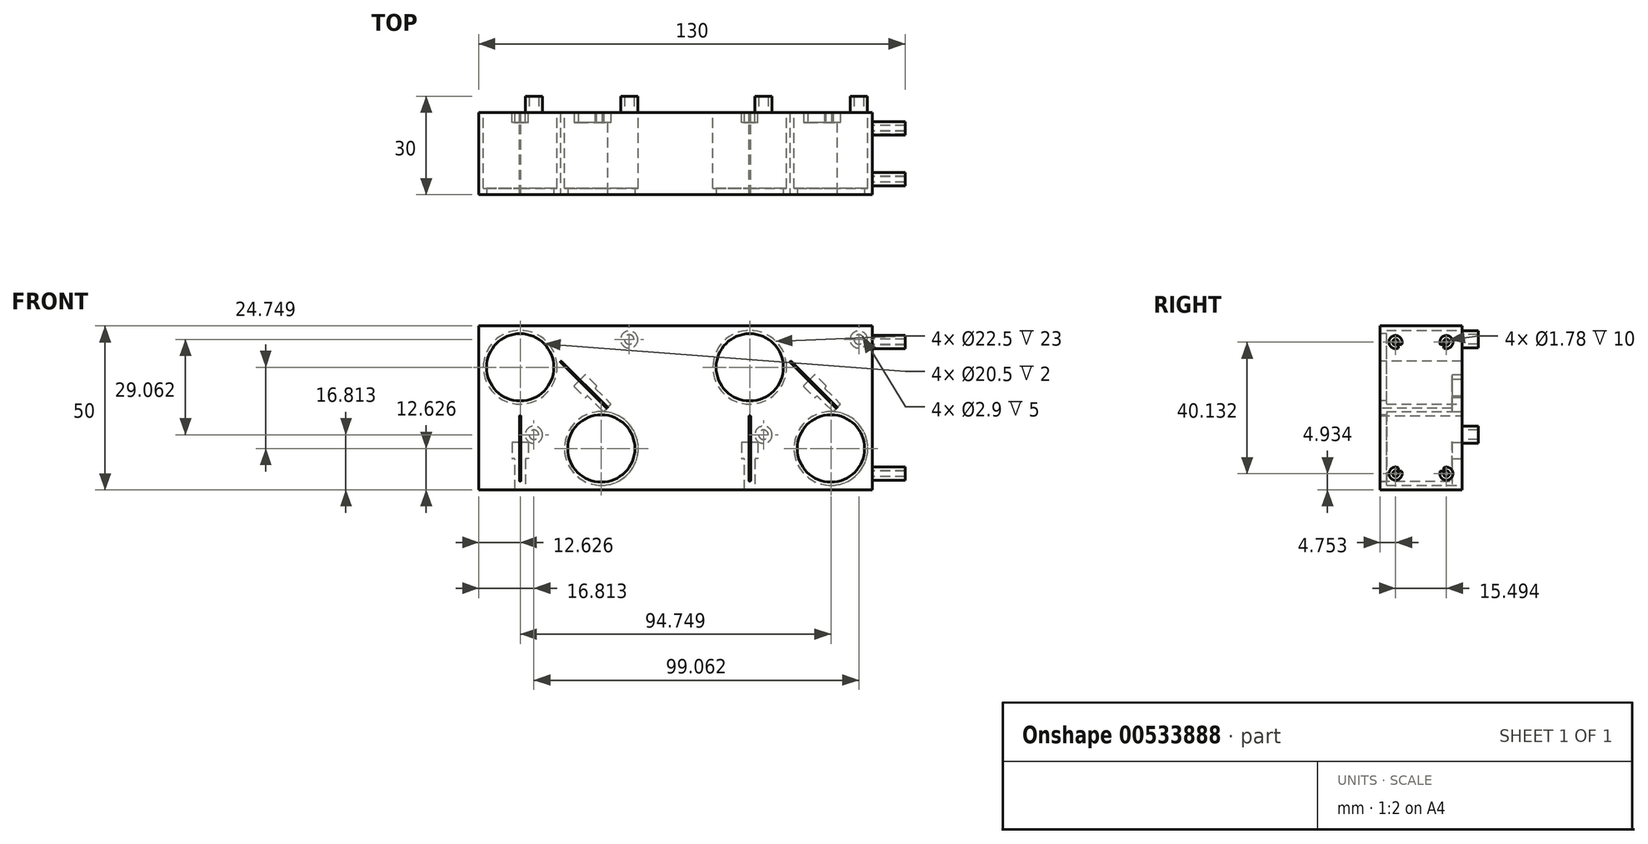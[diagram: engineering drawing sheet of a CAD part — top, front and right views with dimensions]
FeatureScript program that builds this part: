
annotation { "Feature Type Name" : "Feature", "Feature Type Description" : "" }
export const myFeature = defineFeature(function(context is Context, id is Id, definition is map)
    precondition{}
    {
        {
            var Q0;
            Q0=qCreatedBy(makeId("Front.planeOp"),FACE);
            var sketch = newSketch(context, id + "F0", { "sketchPlane" : qUnion([Q0])});
            skLineSegment(sketch, "E0.bottom", {"start": v(-60, 25) * mm, "end": v(60, 25) * mm});
            skLineSegment(sketch, "E0.top", {"start": v(-60, -25) * mm, "end": v(60, -25) * mm});
            skLineSegment(sketch, "E0.left", {"start": v(-60, 25) * mm, "end": v(-60, -25) * mm});
            skLineSegment(sketch, "E0.right", {"start": v(60, 25) * mm, "end": v(60, -25) * mm});
            skPoint(sketch, "E1", {"position": v(-60, 0) * mm});
            skPoint(sketch, "E2", {"position": v(0, 25) * mm});
            skLineSegment(sketch, "E3", {"start": v(0, 25) * mm, "end": v(0, -25) * mm, "construction": true});
            skCircle(sketch, "E4", {"center": v(-47.37, 12.37) * mm, "radius": 11.25 * mm});
            skCircle(sketch, "E5", {"center": v(-22.63, -12.37) * mm, "radius": 11.25 * mm});
            skLineSegment(sketch, "E6", {"start": v(-47.37, 12.37) * mm, "end": v(-22.63, -12.37) * mm, "construction": true});
            skPoint(sketch, "E7", {"position": v(-35, 0) * mm});
            skLineSegment(sketch, "E8.bottom", {"start": v(-47.62, -2.37) * mm, "end": v(-47.12, -2.37) * mm});
            skLineSegment(sketch, "E8.top", {"start": v(-47.62, -22.37) * mm, "end": v(-47.12, -22.37) * mm});
            skLineSegment(sketch, "E8.left", {"start": v(-47.62, -2.37) * mm, "end": v(-47.62, -22.37) * mm});
            skLineSegment(sketch, "E8.right", {"start": v(-47.12, -2.37) * mm, "end": v(-47.12, -22.37) * mm});
            skLineSegment(sketch, "E9", {"start": v(-35.18, 13.97) * mm, "end": v(-34.82, 14.32) * mm});
            skLineSegment(sketch, "E10", {"start": v(-34.82, 14.32) * mm, "end": v(-20.68, 0.18) * mm});
            skLineSegment(sketch, "E11", {"start": v(-20.68, 0.18) * mm, "end": v(-21.03, -0.18) * mm});
            skLineSegment(sketch, "E12", {"start": v(-21.03, -0.18) * mm, "end": v(-35.18, 13.97) * mm});
            skLineSegment(sketch, "E13", {"start": v(-35, 14.14) * mm, "end": v(-20.86, 0) * mm, "construction": true});
            skLineSegment(sketch, "E14", {"start": v(-47.37, -2.37) * mm, "end": v(-47.37, -22.37) * mm, "construction": true});
            skLineSegment(sketch, "E15", {"start": v(-35, 0) * mm, "end": v(-27.93, 7.07) * mm, "construction": true});
            skPoint(sketch, "E16", {"position": v(-47.37, -12.37) * mm});
            skCircle(sketch, "E17.1.0.0", {"center": v(22.63, 12.37) * mm, "radius": 11.25 * mm});
            skLineSegment(sketch, "E17.1.0.1", {"start": v(22.88, -2.37) * mm, "end": v(22.88, -22.37) * mm});
            skLineSegment(sketch, "E17.1.0.2", {"start": v(22.38, -2.37) * mm, "end": v(22.38, -22.37) * mm});
            skLineSegment(sketch, "E17.1.0.3", {"start": v(22.38, -22.37) * mm, "end": v(22.88, -22.37) * mm});
            skLineSegment(sketch, "E17.1.0.4", {"start": v(22.38, -2.37) * mm, "end": v(22.88, -2.37) * mm});
            skLineSegment(sketch, "E17.1.0.5", {"start": v(35.18, 14.32) * mm, "end": v(49.32, 0.18) * mm});
            skLineSegment(sketch, "E17.1.0.6", {"start": v(48.97, -0.18) * mm, "end": v(34.82, 13.97) * mm});
            skLineSegment(sketch, "E17.1.0.7", {"start": v(34.82, 13.97) * mm, "end": v(35.18, 14.32) * mm});
            skLineSegment(sketch, "E17.1.0.8", {"start": v(49.32, 0.18) * mm, "end": v(48.97, -0.18) * mm});
            skCircle(sketch, "E17.1.0.9", {"center": v(47.37, -12.37) * mm, "radius": 11.25 * mm});
            skLineSegment(sketch, "E17.direction1", {"start": v(-47.62, -22.37) * mm, "end": v(22.38, -22.37) * mm, "construction": true});
            skSolve(sketch);
        }
        {
            var Q0;
            Q0 = qSketchRegion(id + "F0", true);
            extrude(context, id + "F1", {"entities" : qUnion([Q0]), "depth" : 25 * mm, "offsetDistance" : 25 * mm});
        }
        {
            var Q0;
            Q0=makeQuery(id+"F1.opExtrude","CAP_FACE",FACE,{"disambiguationData":[OSD([sQuery(id+"F0.wireOp",EDGE,"E0.bottom"),sQuery(id+"F0.wireOp",EDGE,"E0.top"),sQuery(id+"F0.wireOp",EDGE,"E0.left"),sQuery(id+"F0.wireOp",EDGE,"E0.right"),sQuery(id+"F0.wireOp",EDGE,"E4"),sQuery(id+"F0.wireOp",EDGE,"E5"),sQuery(id+"F0.wireOp",EDGE,"E8.bottom"),sQuery(id+"F0.wireOp",EDGE,"E8.top"),sQuery(id+"F0.wireOp",EDGE,"E8.left"),sQuery(id+"F0.wireOp",EDGE,"E8.right"),sQuery(id+"F0.wireOp",EDGE,"E9"),sQuery(id+"F0.wireOp",EDGE,"E10"),sQuery(id+"F0.wireOp",EDGE,"E11"),sQuery(id+"F0.wireOp",EDGE,"E12"),sQuery(id+"F0.wireOp",EDGE,"E17.1.0.0"),sQuery(id+"F0.wireOp",EDGE,"E17.1.0.1"),sQuery(id+"F0.wireOp",EDGE,"E17.1.0.2"),sQuery(id+"F0.wireOp",EDGE,"E17.1.0.3"),sQuery(id+"F0.wireOp",EDGE,"E17.1.0.4"),sQuery(id+"F0.wireOp",EDGE,"E17.1.0.5"),sQuery(id+"F0.wireOp",EDGE,"E17.1.0.6"),sQuery(id+"F0.wireOp",EDGE,"E17.1.0.7"),sQuery(id+"F0.wireOp",EDGE,"E17.1.0.8"),sQuery(id+"F0.wireOp",EDGE,"E17.1.0.9")])],"isStart":false});
            var sketch = newSketch(context, id + "F2", { "sketchPlane" : qUnion([Q0])});
            skCircle(sketch, "E18.0", {"center": v(-47.37, 12.37) * mm, "radius": 11.25 * mm});
            skCircle(sketch, "E18.1", {"center": v(-22.63, -12.37) * mm, "radius": 11.25 * mm});
            skCircle(sketch, "E18.2", {"center": v(22.63, 12.37) * mm, "radius": 11.25 * mm});
            skCircle(sketch, "E18.3", {"center": v(47.37, -12.37) * mm, "radius": 11.25 * mm});
            skCircle(sketch, "E19", {"center": v(-47.37, 12.37) * mm, "radius": 10.25 * mm});
            skCircle(sketch, "E20", {"center": v(-22.63, -12.37) * mm, "radius": 10.25 * mm});
            skCircle(sketch, "E21", {"center": v(22.63, 12.37) * mm, "radius": 10.25 * mm});
            skCircle(sketch, "E22", {"center": v(47.37, -12.37) * mm, "radius": 10.25 * mm});
            skSolve(sketch);
        }
        {
            var Q0;
            Q0 = qSketchRegion(id + "F2", true);
            extrude(context, id + "F3", {"entities" : qUnion([Q0]), "operationType" : NewBodyOperationType.ADD, "oppositeDirection" : true, "depth" : 2 * mm, "offsetDistance" : 25 * mm});
        }
        {
            var Q0;
            Q0=makeQuery(id+"F1.opExtrude","CAP_FACE",FACE,{"disambiguationData":[OSD([sQuery(id+"F0.wireOp",EDGE,"E0.bottom"),sQuery(id+"F0.wireOp",EDGE,"E0.top"),sQuery(id+"F0.wireOp",EDGE,"E0.left"),sQuery(id+"F0.wireOp",EDGE,"E0.right"),sQuery(id+"F0.wireOp",EDGE,"E4"),sQuery(id+"F0.wireOp",EDGE,"E5"),sQuery(id+"F0.wireOp",EDGE,"E8.bottom"),sQuery(id+"F0.wireOp",EDGE,"E8.top"),sQuery(id+"F0.wireOp",EDGE,"E8.left"),sQuery(id+"F0.wireOp",EDGE,"E8.right"),sQuery(id+"F0.wireOp",EDGE,"E9"),sQuery(id+"F0.wireOp",EDGE,"E10"),sQuery(id+"F0.wireOp",EDGE,"E11"),sQuery(id+"F0.wireOp",EDGE,"E12"),sQuery(id+"F0.wireOp",EDGE,"E17.1.0.0"),sQuery(id+"F0.wireOp",EDGE,"E17.1.0.1"),sQuery(id+"F0.wireOp",EDGE,"E17.1.0.2"),sQuery(id+"F0.wireOp",EDGE,"E17.1.0.3"),sQuery(id+"F0.wireOp",EDGE,"E17.1.0.4"),sQuery(id+"F0.wireOp",EDGE,"E17.1.0.5"),sQuery(id+"F0.wireOp",EDGE,"E17.1.0.6"),sQuery(id+"F0.wireOp",EDGE,"E17.1.0.7"),sQuery(id+"F0.wireOp",EDGE,"E17.1.0.8"),sQuery(id+"F0.wireOp",EDGE,"E17.1.0.9")])],"isStart":true});
            var sketch = newSketch(context, id + "F4", { "sketchPlane" : qUnion([Q0])});
            skLineSegment(sketch, "E23.bottom", {"start": v(-25.13, -10.47) * mm, "end": v(-20.13, -10.47) * mm});
            skLineSegment(sketch, "E23.top", {"start": v(-25.13, -15.47) * mm, "end": v(-24.25, -15.47) * mm});
            skLineSegment(sketch, "E23.left", {"start": v(-25.13, -10.47) * mm, "end": v(-25.13, -15.47) * mm});
            skLineSegment(sketch, "E23.right", {"start": v(-20.13, -10.47) * mm, "end": v(-20.13, -15.47) * mm});
            skLineSegment(sketch, "E24", {"start": v(-20.13, -10.47) * mm, "end": v(-25.13, -15.47) * mm, "construction": true});
            skPoint(sketch, "E25", {"position": v(-22.63, -12.97) * mm});
            skLineSegment(sketch, "E26", {"start": v(-24.25, -15.47) * mm, "end": v(-24.25, -25) * mm});
            skLineSegment(sketch, "E27", {"start": v(-24.25, -25) * mm, "end": v(-21, -25) * mm});
            skLineSegment(sketch, "E28", {"start": v(-21, -25) * mm, "end": v(-21, -15.47) * mm});
            skLineSegment(sketch, "E29", {"start": v(-22.63, -12.97) * mm, "end": v(-22.63, -25) * mm, "construction": true});
            skLineSegment(sketch, "E30.trimOffspring", {"start": v(-21, -15.47) * mm, "end": v(-20.13, -15.47) * mm});
            skCircle(sketch, "E31", {"center": v(-22.63, -12.37) * mm, "radius": 0.75 * mm, "construction": true});
            skLineSegment(sketch, "E32", {"start": v(-22.63, -2.37) * mm, "end": v(-22.63, -22.37) * mm, "construction": true});
            skLineSegment(sketch, "E33", {"start": v(-42.5, 10.18) * mm, "end": v(-38.96, 6.65) * mm});
            skLineSegment(sketch, "E34", {"start": v(-38.96, 6.65) * mm, "end": v(-42.5, 3.11) * mm});
            skLineSegment(sketch, "E35", {"start": v(-46.03, 6.65) * mm, "end": v(-42.5, 10.18) * mm});
            skLineSegment(sketch, "E36", {"start": v(-35, 14.14) * mm, "end": v(-49.14, 0) * mm, "construction": true});
            skPoint(sketch, "E37", {"position": v(-40.73, 8.41) * mm});
            skLineSegment(sketch, "E38", {"start": v(-46.03, 6.65) * mm, "end": v(-45.41, 6.03) * mm});
            skLineSegment(sketch, "E39", {"start": v(-45.41, 6.03) * mm, "end": v(-50.3, 1.15) * mm});
            skLineSegment(sketch, "E40", {"start": v(-50.3, 1.15) * mm, "end": v(-48, -1.15) * mm});
            skLineSegment(sketch, "E41", {"start": v(-48, -1.15) * mm, "end": v(-43.11, 3.73) * mm});
            skLineSegment(sketch, "E42", {"start": v(-43.11, 3.73) * mm, "end": v(-42.5, 3.11) * mm});
            skCircle(sketch, "E43", {"center": v(-42.07, 7.07) * mm, "radius": 0.75 * mm, "construction": true});
            skLineSegment(sketch, "E44.1.0.0", {"start": v(24.59, 6.03) * mm, "end": v(19.7, 1.15) * mm});
            skLineSegment(sketch, "E44.1.0.1", {"start": v(23.97, 6.65) * mm, "end": v(24.59, 6.03) * mm});
            skLineSegment(sketch, "E44.1.0.2", {"start": v(23.97, 6.65) * mm, "end": v(27.5, 10.18) * mm});
            skLineSegment(sketch, "E44.1.0.3", {"start": v(27.5, 10.18) * mm, "end": v(31.04, 6.65) * mm});
            skLineSegment(sketch, "E44.1.0.4", {"start": v(31.04, 6.65) * mm, "end": v(27.5, 3.11) * mm});
            skLineSegment(sketch, "E44.1.0.5", {"start": v(26.89, 3.73) * mm, "end": v(27.5, 3.11) * mm});
            skLineSegment(sketch, "E44.1.0.6", {"start": v(22, -1.15) * mm, "end": v(26.89, 3.73) * mm});
            skLineSegment(sketch, "E44.1.0.7", {"start": v(19.7, 1.15) * mm, "end": v(22, -1.15) * mm});
            skLineSegment(sketch, "E44.1.0.8", {"start": v(44.87, -10.47) * mm, "end": v(49.87, -10.47) * mm});
            skLineSegment(sketch, "E44.1.0.9", {"start": v(44.87, -10.47) * mm, "end": v(44.87, -15.47) * mm});
            skLineSegment(sketch, "E44.1.0.10", {"start": v(49.87, -10.47) * mm, "end": v(49.87, -15.47) * mm});
            skLineSegment(sketch, "E44.1.0.11", {"start": v(49, -15.47) * mm, "end": v(49.87, -15.47) * mm});
            skLineSegment(sketch, "E44.1.0.12", {"start": v(49, -25) * mm, "end": v(49, -15.47) * mm});
            skLineSegment(sketch, "E44.1.0.13", {"start": v(45.75, -15.47) * mm, "end": v(45.75, -25) * mm});
            skLineSegment(sketch, "E44.1.0.14", {"start": v(44.87, -15.47) * mm, "end": v(45.75, -15.47) * mm});
            skLineSegment(sketch, "E44.1.0.15", {"start": v(45.75, -25) * mm, "end": v(49, -25) * mm});
            skLineSegment(sketch, "E44.direction1", {"start": v(-24.25, -25) * mm, "end": v(45.75, -25) * mm, "construction": true});
            skSolve(sketch);
        }
        {
            var Q0;
            Q0 = qSketchRegion(id + "F4", true);
            extrude(context, id + "F5", {"entities" : qUnion([Q0]), "operationType" : NewBodyOperationType.REMOVE, "oppositeDirection" : true, "depth" : 3 * mm, "offsetDistance" : 25 * mm});
        }
        {
            var Q0;
            Q0=qCreatedBy(makeId("Front.planeOp"),FACE);
            var sketch = newSketch(context, id + "F6", { "sketchPlane" : qUnion([Q0])});
            skCircle(sketch, "E45", {"center": v(55.87, 20.88) * mm, "radius": 2.62 * mm});
            skCircle(sketch, "E46", {"center": v(26.81, -8.19) * mm, "radius": 2.62 * mm});
            skLineSegment(sketch, "E47", {"start": v(55.88, 20.88) * mm, "end": v(26.81, -8.19) * mm, "construction": true});
            skCircle(sketch, "E48", {"center": v(55.87, 20.88) * mm, "radius": 1.45 * mm});
            skCircle(sketch, "E49", {"center": v(26.81, -8.19) * mm, "radius": 1.45 * mm});
            skCircle(sketch, "E50.1.0.0", {"center": v(-43.19, -8.19) * mm, "radius": 2.62 * mm});
            skCircle(sketch, "E50.1.0.1", {"center": v(-43.19, -8.19) * mm, "radius": 1.45 * mm});
            skCircle(sketch, "E50.1.0.2", {"center": v(-14.13, 20.88) * mm, "radius": 2.62 * mm});
            skCircle(sketch, "E50.1.0.3", {"center": v(-14.13, 20.88) * mm, "radius": 1.45 * mm});
            skLineSegment(sketch, "E50.direction1", {"start": v(26.81, -8.19) * mm, "end": v(-43.19, -8.19) * mm, "construction": true});
            skSolve(sketch);
        }
        {
            var Q0;
            Q0 = qSketchRegion(id + "F6", true);
            extrude(context, id + "F7", {"entities" : qUnion([Q0]), "operationType" : NewBodyOperationType.ADD, "oppositeDirection" : true, "depth" : 5 * mm, "offsetDistance" : 25 * mm});
        }
        {
            var Q0;
            Q0=makeQuery(id+"F1.opExtrude","SWEPT_FACE",FACE,{"disambiguationData":[OSD([sQuery(id+"F0.wireOp",EDGE,"E0.right")])]});
            var sketch = newSketch(context, id + "F8", { "sketchPlane" : qUnion([Q0])});
            skLineSegment(sketch, "E51.bottom", {"start": v(-20.25, 20.07) * mm, "end": v(-4.75, 20.07) * mm, "construction": true});
            skLineSegment(sketch, "E51.top", {"start": v(-20.25, -20.07) * mm, "end": v(-4.75, -20.07) * mm, "construction": true});
            skLineSegment(sketch, "E51.left", {"start": v(-20.25, 20.07) * mm, "end": v(-20.25, -20.07) * mm, "construction": true});
            skLineSegment(sketch, "E51.right", {"start": v(-4.75, 20.07) * mm, "end": v(-4.75, -20.07) * mm, "construction": true});
            skArc(sketch, "E52", {"start": v(-18.41, 19.27) * mm, "mid": v(-21.66, 21.48) * mm, "end": v(-19.45, 18.23) * mm});
            skArc(sketch, "E53", {"start": v(-5.55, 18.23) * mm, "mid": v(-3.34, 21.48) * mm, "end": v(-6.59, 19.27) * mm});
            skArc(sketch, "E54", {"start": v(-6.59, -19.27) * mm, "mid": v(-3.34, -21.48) * mm, "end": v(-5.55, -18.23) * mm});
            skArc(sketch, "E55", {"start": v(-19.45, -18.23) * mm, "mid": v(-21.66, -21.48) * mm, "end": v(-18.41, -19.27) * mm});
            skCircle(sketch, "E56", {"center": v(-20.25, -20.07) * mm, "radius": 0.89 * mm});
            skCircle(sketch, "E57", {"center": v(-4.75, -20.07) * mm, "radius": 0.89 * mm});
            skCircle(sketch, "E58", {"center": v(-4.75, 20.07) * mm, "radius": 0.89 * mm});
            skCircle(sketch, "E59", {"center": v(-20.25, 20.07) * mm, "radius": 0.89 * mm});
            skLineSegment(sketch, "E60", {"start": v(-4.75, 20.07) * mm, "end": v(-20.25, -20.07) * mm, "construction": true});
            skPoint(sketch, "E61", {"position": v(-12.5, 0) * mm});
            skLineSegment(sketch, "E62.0", {"start": v(-19.45, -19.27) * mm, "end": v(-18.41, -19.27) * mm});
            skLineSegment(sketch, "E62.1", {"start": v(-19.45, 19.27) * mm, "end": v(-19.45, 18.23) * mm});
            skLineSegment(sketch, "E62.2", {"start": v(-19.45, 19.27) * mm, "end": v(-18.41, 19.27) * mm});
            skLineSegment(sketch, "E62.3", {"start": v(-5.55, 19.27) * mm, "end": v(-5.55, 18.23) * mm});
            skLineSegment(sketch, "E63.0", {"start": v(-5, -20) * mm, "end": v(-5, 20) * mm, "construction": true});
            skLineSegment(sketch, "E63.1", {"start": v(-20, -20) * mm, "end": v(-5, -20) * mm, "construction": true});
            skLineSegment(sketch, "E63.2", {"start": v(-20, 20) * mm, "end": v(-20, -20) * mm, "construction": true});
            skLineSegment(sketch, "E63.3", {"start": v(-5, 20) * mm, "end": v(-20, 20) * mm, "construction": true});
            skLineSegment(sketch, "E64.trimOffspring", {"start": v(-19.45, -18.23) * mm, "end": v(-19.45, -19.27) * mm});
            skLineSegment(sketch, "E65.trimOffspring", {"start": v(-6.59, 19.27) * mm, "end": v(-5.55, 19.27) * mm});
            skLineSegment(sketch, "E66.trimOffspring", {"start": v(-5.55, -18.23) * mm, "end": v(-5.55, -19.27) * mm});
            skLineSegment(sketch, "E67.trimOffspring", {"start": v(-6.59, -19.27) * mm, "end": v(-5.55, -19.27) * mm});
            skSolve(sketch);
        }
        {
            var Q0;
            Q0=makeQuery(id+"F8.imprint","IMPRINT",FACE,{"disambiguationData":[TD([[makeQuery(id+"F8.imprint","IMPRINT",EDGE,{"derivedFrom":sQuery(id+"F8.wireOp",EDGE,"E53")}),1.0]])]});
            var Q1;
            Q1=makeQuery(id+"F8.imprint","IMPRINT",FACE,{"disambiguationData":[TD([[makeQuery(id+"F8.imprint","IMPRINT",EDGE,{"derivedFrom":sQuery(id+"F8.wireOp",EDGE,"E52")}),1.0]])]});
            var Q2;
            Q2=makeQuery(id+"F8.imprint","IMPRINT",FACE,{"disambiguationData":[TD([[makeQuery(id+"F8.imprint","IMPRINT",EDGE,{"derivedFrom":sQuery(id+"F8.wireOp",EDGE,"E54")}),1.0]])]});
            var Q3;
            Q3=makeQuery(id+"F8.imprint","IMPRINT",FACE,{"disambiguationData":[TD([[makeQuery(id+"F8.imprint","IMPRINT",EDGE,{"derivedFrom":sQuery(id+"F8.wireOp",EDGE,"E55")}),1.0]])]});
            extrude(context, id + "F9", {"entities" : qUnion([Q0, Q1, Q2, Q3]), "operationType" : NewBodyOperationType.ADD, "depth" : 10 * mm, "offsetDistance" : 25 * mm});
        }
        {
            var Q0;
            Q0=makeQuery(id+"F1.opExtrude","SWEPT_EDGE",EDGE,{"disambiguationData":[OSD([sQuery(id+"F0.wireOp",EDGE,"E9"),sQuery(id+"F0.wireOp",EDGE,"E12")])]});
            var Q1;
            Q1=makeQuery(id+"F1.opExtrude","SWEPT_EDGE",EDGE,{"disambiguationData":[OSD([sQuery(id+"F0.wireOp",EDGE,"E9"),sQuery(id+"F0.wireOp",EDGE,"E10")])]});
            var Q2;
            Q2=makeQuery(id+"F1.opExtrude","SWEPT_EDGE",EDGE,{"disambiguationData":[OSD([sQuery(id+"F0.wireOp",EDGE,"E10"),sQuery(id+"F0.wireOp",EDGE,"E11")])]});
            var Q3;
            Q3=makeQuery(id+"F1.opExtrude","SWEPT_EDGE",EDGE,{"disambiguationData":[OSD([sQuery(id+"F0.wireOp",EDGE,"E11"),sQuery(id+"F0.wireOp",EDGE,"E12")])]});
            var Q4;
            Q4=makeQuery(id+"F1.opExtrude","SWEPT_EDGE",EDGE,{"disambiguationData":[OSD([sQuery(id+"F0.wireOp",EDGE,"E8.top"),sQuery(id+"F0.wireOp",EDGE,"E8.right")])]});
            var Q5;
            Q5=makeQuery(id+"F1.opExtrude","SWEPT_EDGE",EDGE,{"disambiguationData":[OSD([sQuery(id+"F0.wireOp",EDGE,"E8.bottom"),sQuery(id+"F0.wireOp",EDGE,"E8.left")])]});
            var Q6;
            Q6=makeQuery(id+"F1.opExtrude","SWEPT_EDGE",EDGE,{"disambiguationData":[OSD([sQuery(id+"F0.wireOp",EDGE,"E8.bottom"),sQuery(id+"F0.wireOp",EDGE,"E8.right")])]});
            var Q7;
            Q7=makeQuery(id+"F1.opExtrude","SWEPT_EDGE",EDGE,{"disambiguationData":[OSD([sQuery(id+"F0.wireOp",EDGE,"E8.top"),sQuery(id+"F0.wireOp",EDGE,"E8.left")])]});
            var Q8;
            Q8=makeQuery(id+"F1.opExtrude","SWEPT_EDGE",EDGE,{"disambiguationData":[OSD([sQuery(id+"F0.wireOp",EDGE,"E17.1.0.2"),sQuery(id+"F0.wireOp",EDGE,"E17.1.0.3")])]});
            var Q9;
            Q9=makeQuery(id+"F1.opExtrude","SWEPT_EDGE",EDGE,{"disambiguationData":[OSD([sQuery(id+"F0.wireOp",EDGE,"E17.1.0.1"),sQuery(id+"F0.wireOp",EDGE,"E17.1.0.3")])]});
            var Q10;
            Q10=makeQuery(id+"F1.opExtrude","SWEPT_EDGE",EDGE,{"disambiguationData":[OSD([sQuery(id+"F0.wireOp",EDGE,"E17.1.0.1"),sQuery(id+"F0.wireOp",EDGE,"E17.1.0.4")])]});
            var Q11;
            Q11=makeQuery(id+"F1.opExtrude","SWEPT_EDGE",EDGE,{"disambiguationData":[OSD([sQuery(id+"F0.wireOp",EDGE,"E17.1.0.2"),sQuery(id+"F0.wireOp",EDGE,"E17.1.0.4")])]});
            var Q12;
            Q12=makeQuery(id+"F1.opExtrude","SWEPT_EDGE",EDGE,{"disambiguationData":[OSD([sQuery(id+"F0.wireOp",EDGE,"E17.1.0.6"),sQuery(id+"F0.wireOp",EDGE,"E17.1.0.7")])]});
            var Q13;
            Q13=makeQuery(id+"F1.opExtrude","SWEPT_EDGE",EDGE,{"disambiguationData":[OSD([sQuery(id+"F0.wireOp",EDGE,"E17.1.0.5"),sQuery(id+"F0.wireOp",EDGE,"E17.1.0.7")])]});
            var Q14;
            Q14=makeQuery(id+"F1.opExtrude","SWEPT_EDGE",EDGE,{"disambiguationData":[OSD([sQuery(id+"F0.wireOp",EDGE,"E17.1.0.6"),sQuery(id+"F0.wireOp",EDGE,"E17.1.0.8")])]});
            var Q15;
            Q15=makeQuery(id+"F1.opExtrude","SWEPT_EDGE",EDGE,{"disambiguationData":[OSD([sQuery(id+"F0.wireOp",EDGE,"E17.1.0.5"),sQuery(id+"F0.wireOp",EDGE,"E17.1.0.8")])]});
            var Q16;
            Q16=makeQuery(id+"F5.boolean.opBoolean","COPY",EDGE,{"derivedFrom":makeQuery(id+"F5.opExtrude","SWEPT_EDGE",EDGE,{"disambiguationData":[OSD([sQuery(id+"F4.wireOp",EDGE,"E39"),sQuery(id+"F4.wireOp",EDGE,"E40")])]})});
            var Q17;
            Q17=makeQuery(id+"F5.boolean.opBoolean","INTERSECT",EDGE,{"derivedFrom":[makeQuery(id+"F1.opExtrude","SWEPT_FACE",FACE,{"disambiguationData":[OSD([sQuery(id+"F0.wireOp",EDGE,"E17.1.0.9")])]}),makeQuery(id+"F5.opExtrude","SWEPT_FACE",FACE,{"disambiguationData":[OSD([sQuery(id+"F4.wireOp",EDGE,"E40")])]})]});
            var Q18;
            Q18=makeQuery(id+"F5.boolean.opBoolean","COPY",EDGE,{"derivedFrom":makeQuery(id+"F5.opExtrude","SWEPT_EDGE",EDGE,{"disambiguationData":[OSD([sQuery(id+"F4.wireOp",EDGE,"E41"),sQuery(id+"F4.wireOp",EDGE,"E42")])]})});
            var Q19;
            Q19=makeQuery(id+"F5.boolean.opBoolean","COPY",EDGE,{"derivedFrom":makeQuery(id+"F5.opExtrude","SWEPT_EDGE",EDGE,{"disambiguationData":[OSD([sQuery(id+"F4.wireOp",EDGE,"E38"),sQuery(id+"F4.wireOp",EDGE,"E39")])]})});
            var Q20;
            Q20=makeQuery(id+"F5.boolean.opBoolean","COPY",EDGE,{"derivedFrom":makeQuery(id+"F5.opExtrude","SWEPT_EDGE",EDGE,{"disambiguationData":[OSD([sQuery(id+"F4.wireOp",EDGE,"E35"),sQuery(id+"F4.wireOp",EDGE,"E38")])]})});
            var Q21;
            Q21=makeQuery(id+"F5.boolean.opBoolean","COPY",EDGE,{"derivedFrom":makeQuery(id+"F5.opExtrude","SWEPT_EDGE",EDGE,{"disambiguationData":[OSD([sQuery(id+"F4.wireOp",EDGE,"E33"),sQuery(id+"F4.wireOp",EDGE,"E35")])]})});
            var Q22;
            Q22=makeQuery(id+"F5.boolean.opBoolean","INTERSECT",EDGE,{"derivedFrom":[makeQuery(id+"F1.opExtrude","SWEPT_FACE",FACE,{"disambiguationData":[OSD([sQuery(id+"F0.wireOp",EDGE,"E17.1.0.5")])]}),makeQuery(id+"F5.opExtrude","SWEPT_FACE",FACE,{"disambiguationData":[OSD([sQuery(id+"F4.wireOp",EDGE,"E33")])]})]});
            var Q23;
            Q23=makeQuery(id+"F5.boolean.opBoolean","INTERSECT",EDGE,{"derivedFrom":[makeQuery(id+"F1.opExtrude","SWEPT_FACE",FACE,{"disambiguationData":[OSD([sQuery(id+"F0.wireOp",EDGE,"E17.1.0.6")])]}),makeQuery(id+"F5.opExtrude","SWEPT_FACE",FACE,{"disambiguationData":[OSD([sQuery(id+"F4.wireOp",EDGE,"E33")])]})]});
            var Q24;
            Q24=makeQuery(id+"F5.boolean.opBoolean","INTERSECT",EDGE,{"derivedFrom":[makeQuery(id+"F1.opExtrude","SWEPT_FACE",FACE,{"disambiguationData":[OSD([sQuery(id+"F0.wireOp",EDGE,"E17.1.0.9")])]}),makeQuery(id+"F5.opExtrude","SWEPT_FACE",FACE,{"disambiguationData":[OSD([sQuery(id+"F4.wireOp",EDGE,"E41")])]})]});
            var Q25;
            Q25=makeQuery(id+"F5.boolean.opBoolean","COPY",EDGE,{"derivedFrom":makeQuery(id+"F5.opExtrude","SWEPT_EDGE",EDGE,{"disambiguationData":[OSD([sQuery(id+"F4.wireOp",EDGE,"E33"),sQuery(id+"F4.wireOp",EDGE,"E34")])]})});
            var Q26;
            Q26=makeQuery(id+"F5.boolean.opBoolean","COPY",EDGE,{"derivedFrom":makeQuery(id+"F5.opExtrude","SWEPT_EDGE",EDGE,{"disambiguationData":[OSD([sQuery(id+"F4.wireOp",EDGE,"E34"),sQuery(id+"F4.wireOp",EDGE,"E42")])]})});
            var Q27;
            Q27=makeQuery(id+"F5.boolean.opBoolean","INTERSECT",EDGE,{"derivedFrom":[makeQuery(id+"F1.opExtrude","SWEPT_FACE",FACE,{"disambiguationData":[OSD([sQuery(id+"F0.wireOp",EDGE,"E17.1.0.2")])]}),makeQuery(id+"F5.opExtrude","SWEPT_FACE",FACE,{"disambiguationData":[OSD([sQuery(id+"F4.wireOp",EDGE,"E23.bottom")])]})]});
            var Q28;
            Q28=makeQuery(id+"F5.boolean.opBoolean","INTERSECT",EDGE,{"derivedFrom":[makeQuery(id+"F1.opExtrude","SWEPT_FACE",FACE,{"disambiguationData":[OSD([sQuery(id+"F0.wireOp",EDGE,"E17.1.0.1")])]}),makeQuery(id+"F5.opExtrude","SWEPT_FACE",FACE,{"disambiguationData":[OSD([sQuery(id+"F4.wireOp",EDGE,"E23.bottom")])]})]});
            var Q29;
            Q29=makeQuery(id+"F5.boolean.opBoolean","COPY",EDGE,{"derivedFrom":makeQuery(id+"F5.opExtrude","SWEPT_EDGE",EDGE,{"disambiguationData":[OSD([sQuery(id+"F4.wireOp",EDGE,"E23.bottom"),sQuery(id+"F4.wireOp",EDGE,"E23.right")])]})});
            var Q30;
            Q30=makeQuery(id+"F5.boolean.opBoolean","COPY",EDGE,{"derivedFrom":makeQuery(id+"F5.opExtrude","SWEPT_EDGE",EDGE,{"disambiguationData":[OSD([sQuery(id+"F4.wireOp",EDGE,"E23.bottom"),sQuery(id+"F4.wireOp",EDGE,"E23.left")])]})});
            var Q31;
            Q31=makeQuery(id+"F5.boolean.opBoolean","COPY",EDGE,{"derivedFrom":makeQuery(id+"F5.opExtrude","SWEPT_EDGE",EDGE,{"disambiguationData":[OSD([sQuery(id+"F4.wireOp",EDGE,"E23.top"),sQuery(id+"F4.wireOp",EDGE,"E26")])]})});
            var Q32;
            Q32=makeQuery(id+"F5.boolean.opBoolean","COPY",EDGE,{"derivedFrom":makeQuery(id+"F5.opExtrude","SWEPT_EDGE",EDGE,{"disambiguationData":[OSD([sQuery(id+"F0.wireOp",EDGE,"E0.top"),sQuery(id+"F4.wireOp",EDGE,"E26"),sQuery(id+"F4.wireOp",EDGE,"E27")])]})});
            var Q33;
            Q33=makeQuery(id+"F5.boolean.opBoolean","COPY",EDGE,{"derivedFrom":makeQuery(id+"F5.opExtrude","SWEPT_EDGE",EDGE,{"disambiguationData":[OSD([sQuery(id+"F0.wireOp",EDGE,"E0.top"),sQuery(id+"F4.wireOp",EDGE,"E27"),sQuery(id+"F4.wireOp",EDGE,"E28")])]})});
            var Q34;
            Q34=makeQuery(id+"F5.boolean.opBoolean","COPY",EDGE,{"derivedFrom":makeQuery(id+"F5.opExtrude","SWEPT_EDGE",EDGE,{"disambiguationData":[OSD([sQuery(id+"F4.wireOp",EDGE,"E23.right"),sQuery(id+"F4.wireOp",EDGE,"E30.trimOffspring")])]})});
            var Q35;
            Q35=makeQuery(id+"F5.boolean.opBoolean","COPY",EDGE,{"derivedFrom":makeQuery(id+"F5.opExtrude","SWEPT_EDGE",EDGE,{"disambiguationData":[OSD([sQuery(id+"F4.wireOp",EDGE,"E28"),sQuery(id+"F4.wireOp",EDGE,"E30.trimOffspring")])]})});
            var Q36;
            Q36=makeQuery(id+"F5.boolean.opBoolean","INTERSECT",EDGE,{"derivedFrom":[makeQuery(id+"F1.opExtrude","SWEPT_FACE",FACE,{"disambiguationData":[OSD([sQuery(id+"F0.wireOp",EDGE,"E12")])]}),makeQuery(id+"F5.opExtrude","SWEPT_FACE",FACE,{"disambiguationData":[OSD([sQuery(id+"F4.wireOp",EDGE,"E44.1.0.3")])]})]});
            var Q37;
            Q37=makeQuery(id+"F5.boolean.opBoolean","INTERSECT",EDGE,{"derivedFrom":[makeQuery(id+"F1.opExtrude","SWEPT_FACE",FACE,{"disambiguationData":[OSD([sQuery(id+"F0.wireOp",EDGE,"E10")])]}),makeQuery(id+"F5.opExtrude","SWEPT_FACE",FACE,{"disambiguationData":[OSD([sQuery(id+"F4.wireOp",EDGE,"E44.1.0.3")])]})]});
            var Q38;
            Q38=makeQuery(id+"F5.boolean.opBoolean","COPY",EDGE,{"derivedFrom":makeQuery(id+"F5.opExtrude","SWEPT_EDGE",EDGE,{"disambiguationData":[OSD([sQuery(id+"F4.wireOp",EDGE,"E44.1.0.3"),sQuery(id+"F4.wireOp",EDGE,"E44.1.0.4")])]})});
            var Q39;
            Q39=makeQuery(id+"F5.boolean.opBoolean","COPY",EDGE,{"derivedFrom":makeQuery(id+"F5.opExtrude","SWEPT_EDGE",EDGE,{"disambiguationData":[OSD([sQuery(id+"F4.wireOp",EDGE,"E44.1.0.5"),sQuery(id+"F4.wireOp",EDGE,"E44.1.0.6")])]})});
            var Q40;
            Q40=makeQuery(id+"F5.boolean.opBoolean","COPY",EDGE,{"derivedFrom":makeQuery(id+"F5.opExtrude","SWEPT_EDGE",EDGE,{"disambiguationData":[OSD([sQuery(id+"F4.wireOp",EDGE,"E44.1.0.2"),sQuery(id+"F4.wireOp",EDGE,"E44.1.0.3")])]})});
            var Q41;
            Q41=makeQuery(id+"F5.boolean.opBoolean","COPY",EDGE,{"derivedFrom":makeQuery(id+"F5.opExtrude","SWEPT_EDGE",EDGE,{"disambiguationData":[OSD([sQuery(id+"F4.wireOp",EDGE,"E44.1.0.0"),sQuery(id+"F4.wireOp",EDGE,"E44.1.0.1")])]})});
            var Q42;
            Q42=makeQuery(id+"F5.boolean.opBoolean","COPY",EDGE,{"derivedFrom":makeQuery(id+"F5.opExtrude","SWEPT_EDGE",EDGE,{"disambiguationData":[OSD([sQuery(id+"F4.wireOp",EDGE,"E44.1.0.0"),sQuery(id+"F4.wireOp",EDGE,"E44.1.0.7")])]})});
            var Q43;
            Q43=makeQuery(id+"F5.boolean.opBoolean","INTERSECT",EDGE,{"derivedFrom":[makeQuery(id+"F1.opExtrude","SWEPT_FACE",FACE,{"disambiguationData":[OSD([sQuery(id+"F0.wireOp",EDGE,"E5")])]}),makeQuery(id+"F5.opExtrude","SWEPT_FACE",FACE,{"disambiguationData":[OSD([sQuery(id+"F4.wireOp",EDGE,"E44.1.0.6")])]})]});
            var Q44;
            Q44=makeQuery(id+"F5.boolean.opBoolean","INTERSECT",EDGE,{"derivedFrom":[makeQuery(id+"F1.opExtrude","SWEPT_FACE",FACE,{"disambiguationData":[OSD([sQuery(id+"F0.wireOp",EDGE,"E5")])]}),makeQuery(id+"F5.opExtrude","SWEPT_FACE",FACE,{"disambiguationData":[OSD([sQuery(id+"F4.wireOp",EDGE,"E44.1.0.7")])]})]});
            var Q45;
            Q45=makeQuery(id+"F5.boolean.opBoolean","COPY",EDGE,{"derivedFrom":makeQuery(id+"F5.opExtrude","SWEPT_EDGE",EDGE,{"disambiguationData":[OSD([sQuery(id+"F4.wireOp",EDGE,"E44.1.0.1"),sQuery(id+"F4.wireOp",EDGE,"E44.1.0.2")])]})});
            var Q46;
            Q46=makeQuery(id+"F5.boolean.opBoolean","COPY",EDGE,{"derivedFrom":makeQuery(id+"F5.opExtrude","SWEPT_EDGE",EDGE,{"disambiguationData":[OSD([sQuery(id+"F4.wireOp",EDGE,"E44.1.0.4"),sQuery(id+"F4.wireOp",EDGE,"E44.1.0.5")])]})});
            var Q47;
            Q47=makeQuery(id+"F5.boolean.opBoolean","COPY",EDGE,{"derivedFrom":makeQuery(id+"F5.opExtrude","SWEPT_EDGE",EDGE,{"disambiguationData":[OSD([sQuery(id+"F4.wireOp",EDGE,"E44.1.0.8"),sQuery(id+"F4.wireOp",EDGE,"E44.1.0.9")])]})});
            var Q48;
            Q48=makeQuery(id+"F5.boolean.opBoolean","INTERSECT",EDGE,{"derivedFrom":[makeQuery(id+"F1.opExtrude","SWEPT_FACE",FACE,{"disambiguationData":[OSD([sQuery(id+"F0.wireOp",EDGE,"E8.right")])]}),makeQuery(id+"F5.opExtrude","SWEPT_FACE",FACE,{"disambiguationData":[OSD([sQuery(id+"F4.wireOp",EDGE,"E44.1.0.8")])]})]});
            var Q49;
            Q49=makeQuery(id+"F5.boolean.opBoolean","INTERSECT",EDGE,{"derivedFrom":[makeQuery(id+"F1.opExtrude","SWEPT_FACE",FACE,{"disambiguationData":[OSD([sQuery(id+"F0.wireOp",EDGE,"E8.left")])]}),makeQuery(id+"F5.opExtrude","SWEPT_FACE",FACE,{"disambiguationData":[OSD([sQuery(id+"F4.wireOp",EDGE,"E44.1.0.8")])]})]});
            var Q50;
            Q50=makeQuery(id+"F5.boolean.opBoolean","COPY",EDGE,{"derivedFrom":makeQuery(id+"F5.opExtrude","SWEPT_EDGE",EDGE,{"disambiguationData":[OSD([sQuery(id+"F4.wireOp",EDGE,"E44.1.0.13"),sQuery(id+"F4.wireOp",EDGE,"E44.1.0.14")])]})});
            var Q51;
            Q51=makeQuery(id+"F5.boolean.opBoolean","COPY",EDGE,{"derivedFrom":makeQuery(id+"F5.opExtrude","SWEPT_EDGE",EDGE,{"disambiguationData":[OSD([sQuery(id+"F4.wireOp",EDGE,"E44.1.0.8"),sQuery(id+"F4.wireOp",EDGE,"E44.1.0.10")])]})});
            var Q52;
            Q52=makeQuery(id+"F5.boolean.opBoolean","COPY",EDGE,{"derivedFrom":makeQuery(id+"F5.opExtrude","SWEPT_EDGE",EDGE,{"disambiguationData":[OSD([sQuery(id+"F4.wireOp",EDGE,"E44.1.0.11"),sQuery(id+"F4.wireOp",EDGE,"E44.1.0.12")])]})});
            var Q53;
            Q53=makeQuery(id+"F5.boolean.opBoolean","COPY",EDGE,{"derivedFrom":makeQuery(id+"F5.opExtrude","SWEPT_EDGE",EDGE,{"disambiguationData":[OSD([sQuery(id+"F4.wireOp",EDGE,"E44.1.0.10"),sQuery(id+"F4.wireOp",EDGE,"E44.1.0.11")])]})});
            var Q54;
            Q54=makeQuery(id+"F5.boolean.opBoolean","COPY",EDGE,{"derivedFrom":makeQuery(id+"F5.opExtrude","SWEPT_EDGE",EDGE,{"disambiguationData":[OSD([sQuery(id+"F0.wireOp",EDGE,"E0.top"),sQuery(id+"F4.wireOp",EDGE,"E44.1.0.12"),sQuery(id+"F4.wireOp",EDGE,"E44.1.0.15")])]})});
            var Q55;
            Q55=makeQuery(id+"F5.boolean.opBoolean","COPY",EDGE,{"derivedFrom":makeQuery(id+"F5.opExtrude","SWEPT_EDGE",EDGE,{"disambiguationData":[OSD([sQuery(id+"F0.wireOp",EDGE,"E0.top"),sQuery(id+"F4.wireOp",EDGE,"E44.1.0.13"),sQuery(id+"F4.wireOp",EDGE,"E44.1.0.15")])]})});
            fillet(context, id + "F10", {"entities" : qUnion([Q0, Q1, Q2, Q3, Q4, Q5, Q6, Q7, Q8, Q9, Q10, Q11, Q12, Q13, Q14, Q15, Q16, Q17, Q18, Q19, Q20, Q21, Q22, Q23, Q24, Q25, Q26, Q27, Q28, Q29, Q30, Q31, Q32, Q33, Q34, Q35, Q36, Q37, Q38, Q39, Q40, Q41, Q42, Q43, Q44, Q45, Q46, Q47, Q48, Q49, Q50, Q51, Q52, Q53, Q54, Q55]), "radius" : .2 * mm, "tangentPropagation" : true, "allowEdgeOverflow" : false});
        }
    });
